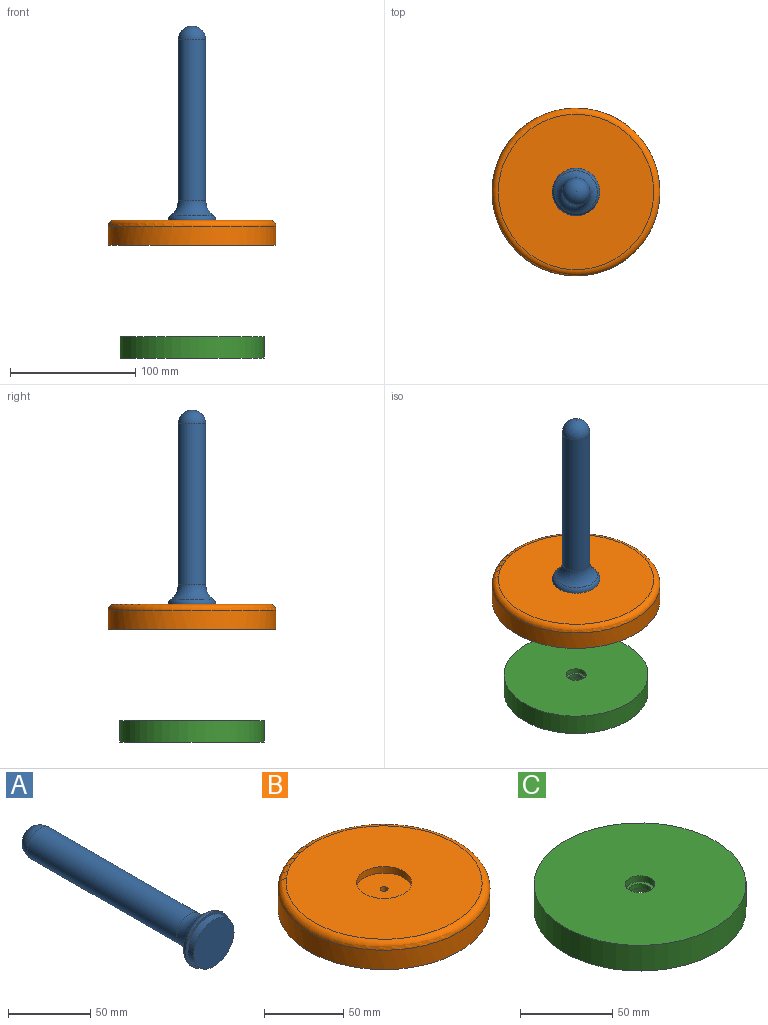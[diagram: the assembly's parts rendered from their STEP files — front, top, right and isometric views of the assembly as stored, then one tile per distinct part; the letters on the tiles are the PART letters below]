
ASSEMBLY  parts=3 mates=3
PART A: 7 faces, bbox 56.3x160x56.3 mm
  f0: plane 38x38mm, normal (0,-1,0), area 199.3mm2, adj f1,f6
  f1: cylinder r=17.25mm len=34.5mm, axis (0,1,0), area 541.9mm2, adj f0,f2
  f2: plane 34.5x34.5mm, normal (0,-1,0), area 934.8mm2, adj f1
  f3: sphere r=11mm, area 760.3mm2, adj f4
  f4: cylinder r=11mm len=128mm, axis (0,1,0), area 8846.7mm2, adj f3,f5
  f5: torus R=26mm, axis (0,1,0), area 1141.3mm2, adj f4,f6
  f6: torus R=14mm, axis (0,1,0), area 533.5mm2, adj f0,f5
PART B: 11 faces, bbox 145x145x20 mm
  f0: plane 134x134mm, normal (0,0,-1), area 2792.9mm2, adj f1,f9
  f1: cylinder r=60mm len=120mm, axis (0,0,1), area 4146.9mm2, adj f0,f2
  f2: plane 120x120mm, normal (0,0,-1), area 3455.8mm2, adj f1,f3
  f3: cone r=50mm half-angle=83.9deg, axis (0,0,1), area 7404.9mm2, adj f2,f4
  f4: plane 25x25mm, normal (0,0,-1), area 471.2mm2, adj f3,f5
  f5: cylinder r=2.5mm len=8mm, axis (0,0,1), area 125.7mm2, adj f4,f6
  f6: plane 35x35mm, normal (0,0,1), area 942.5mm2, adj f5,f7
  f7: cylinder r=17.5mm len=35mm, axis (0,0,1), area 549.8mm2, adj f6,f8
  f8: plane 124x124mm, normal (0,0,1), area 11114.2mm2, adj f7,f10
  f9: cylinder r=67mm len=134mm, axis (0,0,1), area 6314.6mm2, adj f0,f10
  f10: torus R=62mm, axis (0,0,-1), area 3216.7mm2, adj f8,f9
PART C: 10 faces, bbox 115x115x17 mm
  f0: plane 16x16mm, normal (0,0,1), area 88mm2, adj f1,f9
  f1: cylinder r=8mm len=16mm, axis (0,0,1), area 201.1mm2, adj f0,f2
  f2: plane 115x115mm, normal (0,0,1), area 10185.8mm2, adj f1,f3
  f3: cylinder r=57.5mm len=115mm, axis (0,0,1), area 6141.8mm2, adj f2,f4
  f4: plane 115x115mm, normal (0,0,-1), area 9424.8mm2, adj f3,f5
  f5: cylinder r=17.5mm len=35mm, axis (0,0,1), area 659.7mm2, adj f4,f6
  f6: plane 35x35mm, normal (0,0,-1), area 761.1mm2, adj f5,f7
  f7: cylinder r=8mm len=16mm, axis (0,0,1), area 201.1mm2, adj f6,f8
  f8: plane 16x16mm, normal (0,0,-1), area 88mm2, adj f7,f9
  f9: cylinder r=6mm len=12mm, axis (0,0,1), area 113.1mm2, adj f0,f8
PLACE A rot(axis=(1,0,0),90deg) t=(0,0,105)mm
PLACE B t=(0,0,90)mm
PLACE C at identity
MATE slider B.f1 <-> C.f1  axis (0,0,1) through (0,0,107.5)mm
MATE slider A.f1 <-> B.f1  axis (0,0,1) through (0,0,190)mm
MATE parallel B.f1 <-> A.f1  axis (0,0,1) through (0,0,105)mm
